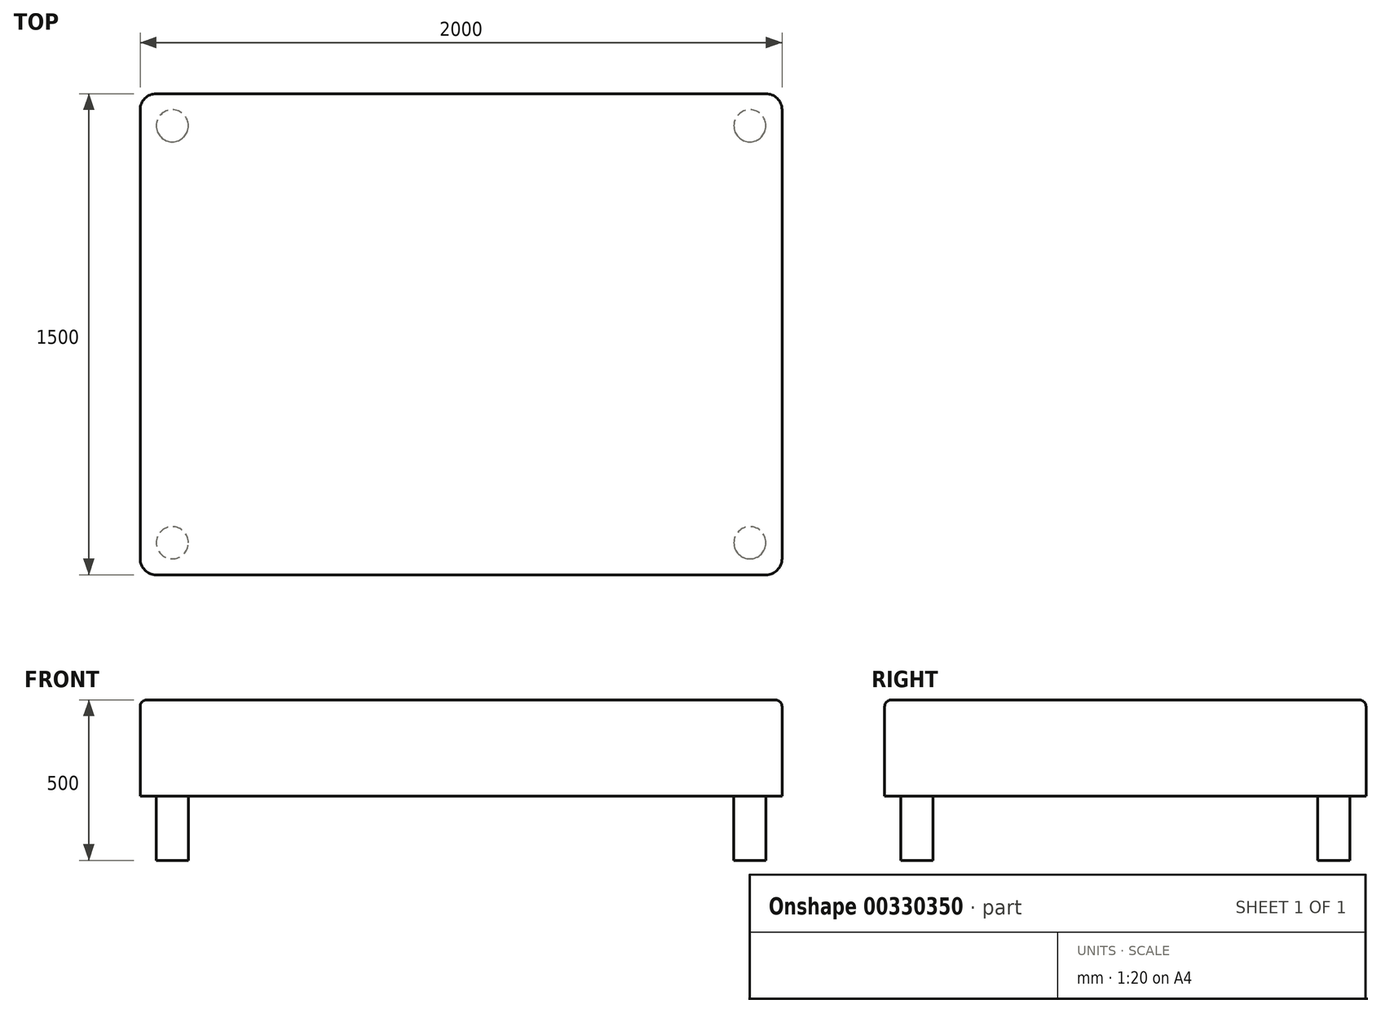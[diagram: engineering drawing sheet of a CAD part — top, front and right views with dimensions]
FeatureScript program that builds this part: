
annotation { "Feature Type Name" : "Feature", "Feature Type Description" : "" }
export const myFeature = defineFeature(function(context is Context, id is Id, definition is map)
    precondition{}
    {
        {
            var Q0;
            Q0=qCreatedBy(makeId("Top.planeOp"),FACE);
            var sketch = newSketch(context, id + "F0", { "sketchPlane" : qUnion([Q0])});
            skLineSegment(sketch, "E0.bottom", {"start": v(0, 0) * mm, "end": v(2000, 0) * mm});
            skLineSegment(sketch, "E0.top", {"start": v(0, 1500) * mm, "end": v(2000, 1500) * mm});
            skLineSegment(sketch, "E0.left", {"start": v(0, 0) * mm, "end": v(0, 1500) * mm});
            skLineSegment(sketch, "E0.right", {"start": v(2000, 0) * mm, "end": v(2000, 1500) * mm});
            skSolve(sketch);
        }
        {
            var Q0;
            Q0 = qSketchRegion(id + "F0", true);
            extrude(context, id + "F1", {"entities" : qUnion([Q0]), "depth" : 300 * mm});
        }
        {
            var Q0;
            Q0=makeQuery(id+"F1.opExtrude","SWEPT_EDGE",EDGE,{"disambiguationData":[OSD([sQuery(id+"F0.wireOp",EDGE,"E0.bottom"),sQuery(id+"F0.wireOp",EDGE,"E0.right")])]});
            var Q1;
            Q1=makeQuery(id+"F1.opExtrude","SWEPT_EDGE",EDGE,{"disambiguationData":[OSD([sQuery(id+"F0.wireOp",EDGE,"E0.top"),sQuery(id+"F0.wireOp",EDGE,"E0.right")])]});
            var Q2;
            Q2=makeQuery(id+"F1.opExtrude","SWEPT_EDGE",EDGE,{"disambiguationData":[OSD([sQuery(id+"F0.wireOp",EDGE,"E0.bottom"),sQuery(id+"F0.wireOp",EDGE,"E0.left")])]});
            var Q3;
            Q3=makeQuery(id+"F1.opExtrude","SWEPT_EDGE",EDGE,{"disambiguationData":[OSD([sQuery(id+"F0.wireOp",EDGE,"E0.top"),sQuery(id+"F0.wireOp",EDGE,"E0.left")])]});
            fillet(context, id + "F2", {"entities" : qUnion([Q0, Q1, Q2, Q3]), "radius" : 50 * mm, "tangentPropagation" : true, "allowEdgeOverflow" : false});
        }
        {
            var Q0;
            Q0=makeQuery(id+"F1.opExtrude","CAP_FACE",FACE,{"disambiguationData":[OSD([sQuery(id+"F0.wireOp",EDGE,"E0.bottom"),sQuery(id+"F0.wireOp",EDGE,"E0.top"),sQuery(id+"F0.wireOp",EDGE,"E0.left"),sQuery(id+"F0.wireOp",EDGE,"E0.right")])],"isStart":false});
            fillet(context, id + "F3", {"entities" : qUnion([Q0]), "radius" : 20 * mm, "tangentPropagation" : true, "allowEdgeOverflow" : false});
        }
        {
            var Q0;
            Q0=makeQuery(id+"F1.opExtrude","CAP_FACE",FACE,{"disambiguationData":[OSD([sQuery(id+"F0.wireOp",EDGE,"E0.bottom"),sQuery(id+"F0.wireOp",EDGE,"E0.top"),sQuery(id+"F0.wireOp",EDGE,"E0.left"),sQuery(id+"F0.wireOp",EDGE,"E0.right")])],"isStart":true});
            var sketch = newSketch(context, id + "F4", { "sketchPlane" : qUnion([Q0])});
            skCircle(sketch, "E1", {"center": v(100, -100) * mm, "radius": 50 * mm});
            skCircle(sketch, "E2.0.1.0", {"center": v(100, -1400) * mm, "radius": 50 * mm});
            skCircle(sketch, "E2.1.0.0", {"center": v(1900, -100) * mm, "radius": 50 * mm});
            skCircle(sketch, "E2.1.1.0", {"center": v(1900, -1400) * mm, "radius": 50 * mm});
            skLineSegment(sketch, "E2.direction1", {"start": v(100, -100) * mm, "end": v(1900, -100) * mm, "construction": true});
            skLineSegment(sketch, "E2.direction2", {"start": v(100, -100) * mm, "end": v(100, -1400) * mm, "construction": true});
            skSolve(sketch);
        }
        {
            var Q0;
            Q0 = qSketchRegion(id + "F4", true);
            extrude(context, id + "F5", {"entities" : qUnion([Q0]), "operationType" : NewBodyOperationType.ADD, "depth" : 200 * mm});
        }
    });
